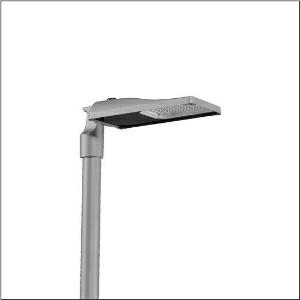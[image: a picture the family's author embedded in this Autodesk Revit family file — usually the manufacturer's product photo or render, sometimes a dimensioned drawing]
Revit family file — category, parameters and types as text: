
# Revit family: streetlight_sl_31_mini___st1_0a_5xh2d3as08ja_29fe
name_source: partatom
category: Lighting Fixtures
units: mm (PartAtom-declared; Revit-internal decimal feet)

## family parameters
Cut with Voids When Loaded = No
Host = Face
Light Source = No
Part Type = Normal
Room Calculation Point = No
Round Connector Dimension = Use Diameter
Shared = No

## types (1)
- --- (1 x LED, 12270 lm, 82.5 W, 3000K)
    Apparent Load = 83 VA
    CIE Flux Codes = 40 73 97 100 100
    Color Rendering = 70
    Color Temperature = 3000K
    Default Elevation = 1800 mm
    Description = Streetlight SL 31 mini D4i mast luminaire for post-top, side-entry; light control with lens of PMMA; light distribution: ST1.0a, direct asymmetric distribution, for standard-compliant lighting for roads and squares; LED: luminous flux: 12.270lm, light colour: 730, colour temperature: 3000K; luminous efficacy: 148,7lm/W; control: pre-setting: logarithmic dimming characteristic, flexible luminous flux parameterisation, time-dependent luminous flux control, constant luminous flux control, power reduction, intelligent temperature release in ECG and LED module, overheat protection; luminaire housing, of diecast aluminium, Siteco® metallic grey (DB 702S), corrosivity category C5 high according to DIN EN ISO 12944; cover of toughened safety glass, transparent, mast flange of diecast aluminium, Siteco® metallic grey (DB 702S), spigot size: 76/60mm, mast flange included unmounted; with cable H07RN-F 2x 1.5mm², cable length: 10,5m, connection cable pre-assembled; mains connection: 220..240V, AC, 50/60Hz; power consumption (at start of service life): 82,5W / (at end of service life): 90,1W / (with reduced operation 50%): 36,8W; protection rating (complete): IP66; insulation class (complete): insulation class II (safety insulation); impact resistance: IK10; certification: CE, ENEC, ENEC+, VDE, UKCA, ZD4i; permissible operating ambient temperature for outdoor applications: -40..+50°C; packaging unit: 1 piece

Light Distribution: ST1.0a
    Height = 76 mm
    Lamp = 1 x LED
    Lamp Light Flux = 12270 lm
    Lamp Power = 82.5 W
    Lamp count = 1
    Length = 547 mm
    Luminous efficacy = 149 lm/W
    Manufacturer = Siteco
    ModVariant = No
    Model = 5XH2D3AS08JA
    Number of Poles = 1
    OnlyDefault = Yes
    Power Factor = 1
    Product Name = Streetlight SL 31 mini | ST1.0a
    Product group = mast luminaire | pylon top
    ProductGroupID = 6100
    Protection Class = Protection class II
    Protection Degree = IP 66
    RLX_Detail_Level = 1
    RLX_Emergency_Light_Flux = 0 lm
    RLX_Emergency_Type = 0
    RLX_Emergency_Type_DB = No
    RlxData = <blob elided: 39693 chars, md5=121f4ad1>
    Socket = socket
    Standby Power = 0 W
    System Light Flux = 12270 lm
    System Power = 83 W
    Type Comments = factory setting: luminous flux: 100 % | dim-lin: 254 | 870 mA
    Type Image = l_1300330.jpg
    URL = http://relux.com
    VarID = @adj_050846
    Voltage = 0 V
    Weight = 0.00 kg
    Width = 265 mm

## geometry (parser evidence)
native form markers: Blend x4, Sweep x8
no freeform markers — native parametric forms only
